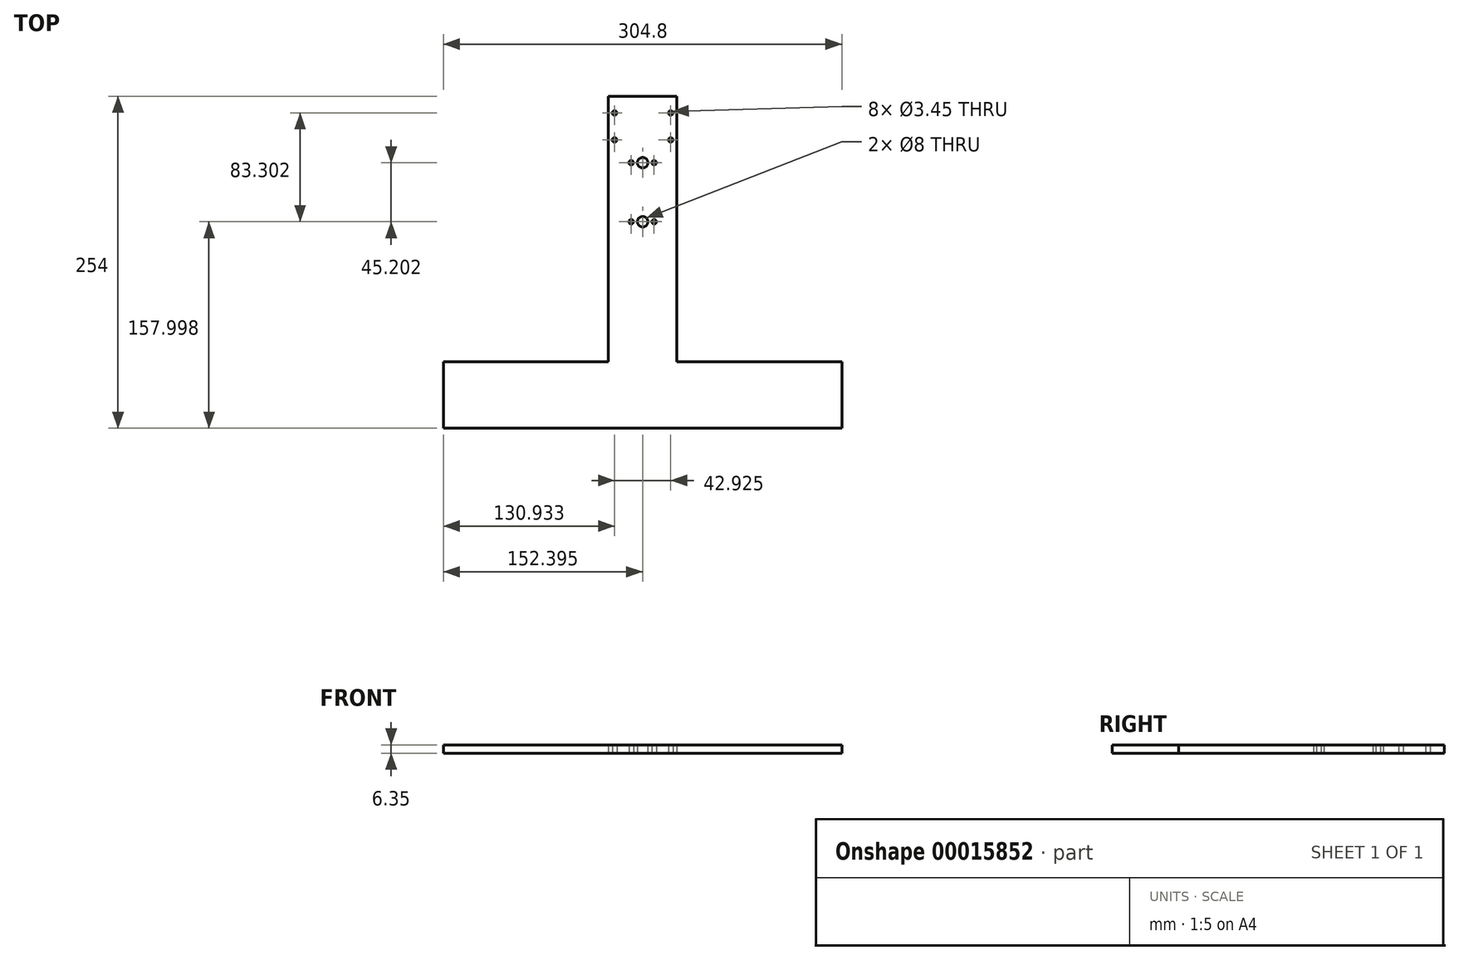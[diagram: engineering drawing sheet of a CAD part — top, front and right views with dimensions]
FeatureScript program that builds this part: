
annotation { "Feature Type Name" : "Feature", "Feature Type Description" : "" }
export const myFeature = defineFeature(function(context is Context, id is Id, definition is map)
    precondition{}
    {
        {
            var Q0;
            Q0=qCreatedBy(makeId("Top.planeOp"),FACE);
            var sketch = newSketch(context, id + "F0", { "sketchPlane" : qUnion([Q0])});
            skLineSegment(sketch, "E0.bottom", {"start": v(0, 0) * mm, "end": v(52.45, 0) * mm});
            skLineSegment(sketch, "E0.top", {"start": v(0, -203.2) * mm, "end": v(52.45, -203.2) * mm});
            skLineSegment(sketch, "E0.left", {"start": v(0, 0) * mm, "end": v(0, -203.2) * mm});
            skLineSegment(sketch, "E0.right", {"start": v(52.45, 0) * mm, "end": v(52.45, -203.2) * mm});
            skLineSegment(sketch, "E1", {"start": v(26.23, 0) * mm, "end": v(26.23, -50.8) * mm});
            skLineSegment(sketch, "E2.top", {"start": v(0, -12.7) * mm, "end": v(4.76, -12.7) * mm});
            skLineSegment(sketch, "E2.right", {"start": v(4.76, 0) * mm, "end": v(4.76, -12.7) * mm});
            skLineSegment(sketch, "E3.bottom", {"start": v(47.69, -12.7) * mm, "end": v(52.45, -12.7) * mm});
            skLineSegment(sketch, "E3.left", {"start": v(47.69, -12.7) * mm, "end": v(47.69, 0) * mm});
            skCircle(sketch, "E4", {"center": v(26.23, -50.8) * mm, "radius": 4 * mm});
            skLineSegment(sketch, "E5", {"start": v(4.76, -12.7) * mm, "end": v(4.76, -33.34) * mm});
            skLineSegment(sketch, "E6", {"start": v(47.69, -12.7) * mm, "end": v(47.69, -33.34) * mm});
            skLineSegment(sketch, "E7", {"start": v(17.46, -50.8) * mm, "end": v(34.99, -50.8) * mm});
            skCircle(sketch, "E8", {"center": v(4.76, -12.7) * mm, "radius": 1.73 * mm});
            skCircle(sketch, "E9", {"center": v(4.76, -33.34) * mm, "radius": 1.73 * mm});
            skCircle(sketch, "E10", {"center": v(47.69, -33.34) * mm, "radius": 1.73 * mm});
            skCircle(sketch, "E11", {"center": v(47.69, -12.7) * mm, "radius": 1.73 * mm});
            skCircle(sketch, "E12", {"center": v(34.99, -50.8) * mm, "radius": 1.73 * mm});
            skCircle(sketch, "E13", {"center": v(17.46, -50.8) * mm, "radius": 1.73 * mm});
            skLineSegment(sketch, "E14", {"start": v(26.23, -50.8) * mm, "end": v(26.23, -96) * mm});
            skLineSegment(sketch, "E15", {"start": v(17.46, -96) * mm, "end": v(34.99, -96) * mm});
            skCircle(sketch, "E16", {"center": v(26.23, -96) * mm, "radius": 4 * mm});
            skCircle(sketch, "E17", {"center": v(17.46, -96) * mm, "radius": 1.73 * mm});
            skCircle(sketch, "E18", {"center": v(34.99, -96) * mm, "radius": 1.73 * mm});
            skLineSegment(sketch, "E19.top", {"start": v(-126.17, -254) * mm, "end": v(178.63, -254) * mm});
            skLineSegment(sketch, "E19.left", {"start": v(-126.17, -203.2) * mm, "end": v(-126.17, -254) * mm});
            skLineSegment(sketch, "E19.right", {"start": v(178.63, -203.2) * mm, "end": v(178.63, -254) * mm});
            skLineSegment(sketch, "E20", {"start": v(-126.17, -203.2) * mm, "end": v(0, -203.2) * mm});
            skLineSegment(sketch, "E21", {"start": v(178.63, -203.2) * mm, "end": v(52.45, -203.2) * mm});
            skSolve(sketch);
        }
        {
            var Q0;
            Q0 = qSketchRegion(id + "F0", true);
            extrude(context, id + "F1", {"entities" : qUnion([Q0]), "depth" : 6.35 * mm});
        }
    });
